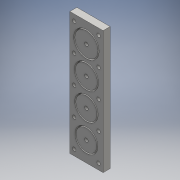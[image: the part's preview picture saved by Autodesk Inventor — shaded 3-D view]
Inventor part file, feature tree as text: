
AUTODESK INVENTOR PART (.ipt)
format: ipt  version: 2016 (Build 200138000, 138)  size: 172,544 bytes
history: native  units: mm
features: extrude x1, sketch x1
ambient origin geometry x8: Origin, YZ Plane, XZ Plane, XY Plane, X Axis, Y Axis, Z Axis, Center Point
bodies: Body1 (feature_tree)
feature tree (2):
  extrude  "Extrusion3"  Depth=6.39mm
  sketch  "Sketch1"  dims[d0=20.9mm d1=3.175mm d2=19.8mm d3=3.175mm d4=19.14mm d5=3.175mm d6=18.7mm d7=3.175mm d8=25.0mm d9=25.0mm d10=25.0mm d11=15.0mm d12=15.0mm d13=18.0mm d14=18.0mm d15=1.0mm d16=1.0mm d17=1.0mm d18=1.0mm d19=3.175mm d20=4.0mm d25=6.39mm d26=0.0mm]
